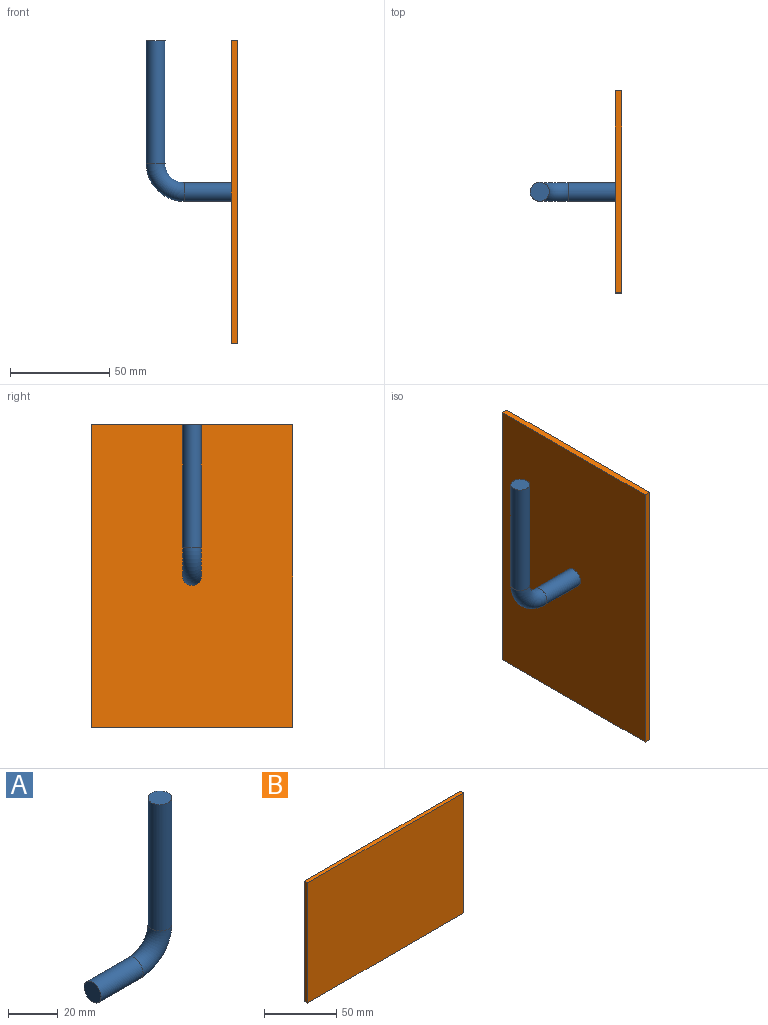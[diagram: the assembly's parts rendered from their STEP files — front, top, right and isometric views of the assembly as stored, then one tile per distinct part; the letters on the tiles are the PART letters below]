
ASSEMBLY  parts=2 mates=1
PART A: 5 faces, bbox 44.4x9.5x82.5 mm
  f0: plane 9.53x9.53mm, normal (-1,0,0), area 71.3mm2, adj f2
  f1: plane 9.53x9.53mm, normal (0,0,1), area 71.3mm2, adj f4
  f2: cylinder r=4.76mm len=23.81mm, axis (1,0,0), area 712.6mm2, adj f0,f3
  f3: torus R=14.29mm, axis (0,-1,0), area 671.6mm2, adj f2,f4
  f4: cylinder r=4.76mm len=61.91mm, axis (0,0,1), area 1852.6mm2, adj f1,f3
PART B: 6 faces, bbox 152.4x3.2x101.6 mm
  f0: plane 152.4x3.18mm, normal (0,0,1), area 483.9mm2, adj f1,f3,f4,f5
  f1: plane 101.6x3.18mm, normal (-1,0,0), area 322.6mm2, adj f0,f2,f4,f5
  f2: plane 152.4x3.18mm, normal (0,0,-1), area 483.9mm2, adj f1,f3,f4,f5
  f3: plane 101.6x3.18mm, normal (1,0,0), area 322.6mm2, adj f0,f2,f4,f5
  f4: plane 152.4x101.6mm, normal (0,-1,0), area 15483.8mm2, adj f0,f1,f2,f3
  f5: plane 152.4x101.6mm, normal (0,1,0), area 15483.8mm2, adj f0,f1,f2,f3
PLACE A rot(axis=(0,0,1),180deg) t=(79.25,121.31,-32.04)mm
PLACE B rot(axis=(0.58,-0.58,0.58),120deg) t=(80.84,121.31,-32.04)mm
MATE fastened B.f5 <-> A.f2  axis (1,0,0) through (79.25,121.31,-32.04)mm
